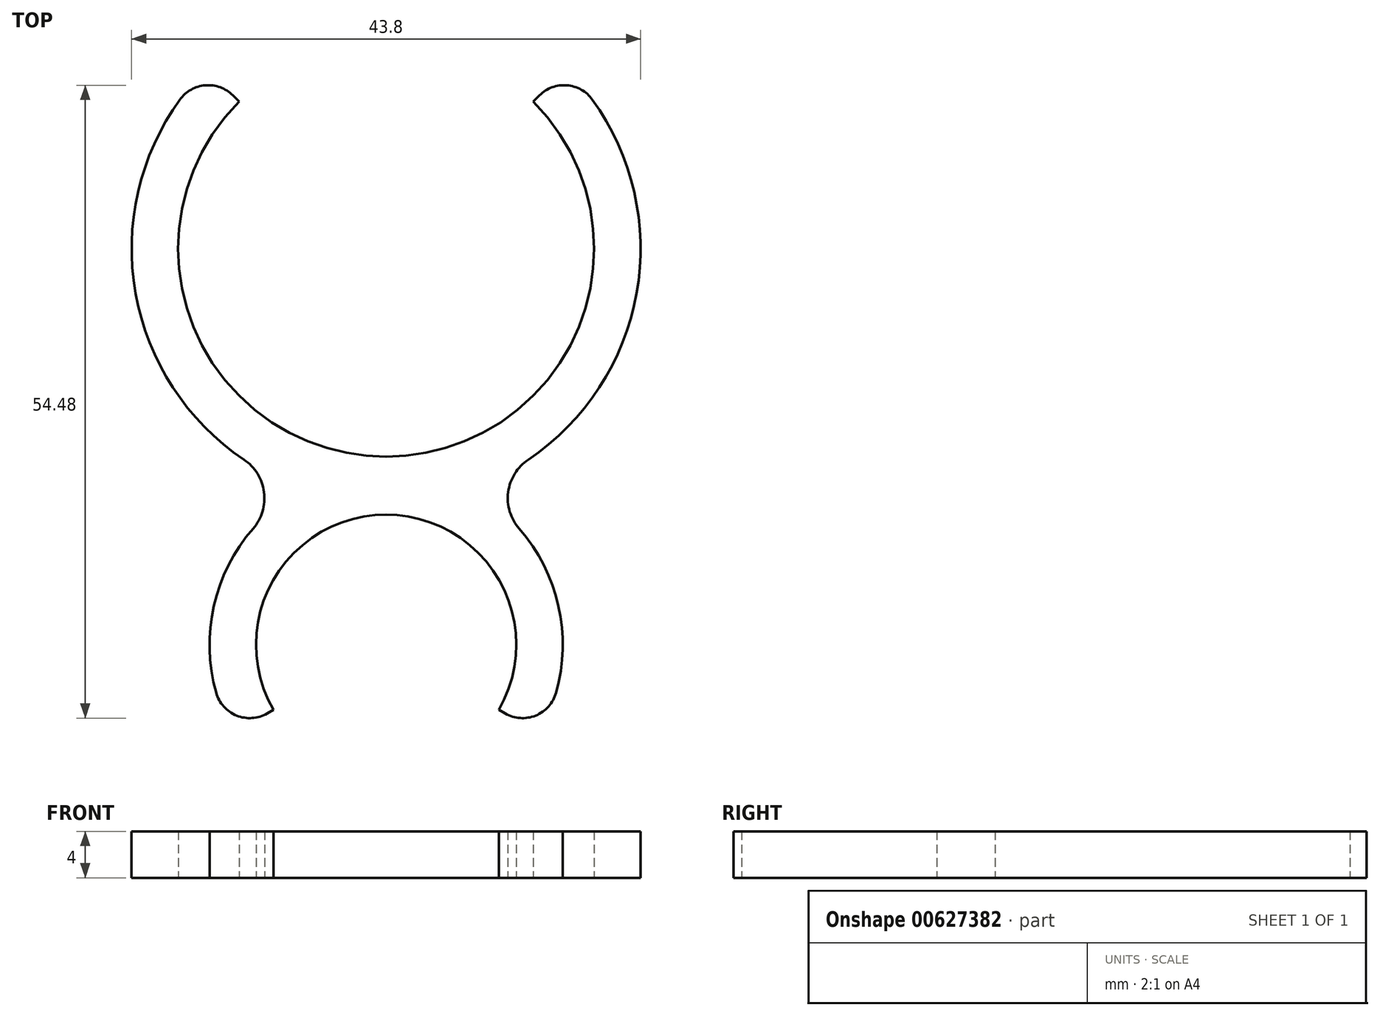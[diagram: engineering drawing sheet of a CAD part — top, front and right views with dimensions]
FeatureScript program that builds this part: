
annotation { "Feature Type Name" : "Feature", "Feature Type Description" : "" }
export const myFeature = defineFeature(function(context is Context, id is Id, definition is map)
    precondition{}
    {
        {
            var Q0;
            Q0=qCreatedBy(makeId("Top.planeOp"),FACE);
            var sketch = newSketch(context, id + "F0", { "sketchPlane" : qUnion([Q0])});
            skLineSegment(sketch, "E0", {"start": v(0, 20.4) * mm, "end": v(0, -13.7) * mm, "construction": true});
            skArc(sketch, "E1", {"start": v(-12.66, 33.06) * mm, "mid": v(0, 2.5) * mm, "end": v(12.66, 33.06) * mm});
            skArc(sketch, "E2", {"start": v(9.7, -19.3) * mm, "mid": v(0, -2.5) * mm, "end": v(-9.7, -19.3) * mm});
            skLineSegment(sketch, "E3", {"start": v(0, -2.5) * mm, "end": v(0, 2.5) * mm, "construction": true});
            skArc(sketch, "E4", {"start": v(-11.46, -3.7) * mm, "mid": v(-14.83, -10.37) * mm, "end": v(-14.63, -17.83) * mm});
            skArc(sketch, "E5", {"start": v(12.24, 2.24) * mm, "mid": v(21.56, 16.57) * mm, "end": v(17.75, 33.23) * mm});
            skPoint(sketch, "E6.visualSharp", {"position": v(-7.17, -0.3) * mm});
            skArc(sketch, "E6.filletArc", {"start": v(-11.46, -3.7) * mm, "mid": v(-10.5, -0.56) * mm, "end": v(-12.24, 2.24) * mm});
            skPoint(sketch, "E7.visualSharp", {"position": v(7.17, -0.3) * mm});
            skArc(sketch, "E7.filletArc", {"start": v(12.24, 2.24) * mm, "mid": v(10.5, -0.56) * mm, "end": v(11.46, -3.7) * mm});
            skLineSegment(sketch, "E8", {"start": v(0, -13.7) * mm, "end": v(-10.24, -19.61) * mm});
            skLineSegment(sketch, "E9", {"start": v(0, 20.4) * mm, "end": v(-13.2, 33.6) * mm});
            skArc(sketch, "E10.MirrorC", {"start": v(-9.7, -19.3) * mm, "mid": v(0, -2.5) * mm, "end": v(9.7, -19.3) * mm});
            skArc(sketch, "E11.MirrorC", {"start": v(12.66, 33.06) * mm, "mid": v(0, 2.5) * mm, "end": v(-12.66, 33.06) * mm});
            skLineSegment(sketch, "E12.MirrorCS", {"start": v(12.66, 33.06) * mm, "end": v(13.2, 33.6) * mm});
            skLineSegment(sketch, "E13.MirrorCS", {"start": v(9.7, -19.3) * mm, "end": v(10.24, -19.61) * mm});
            skArc(sketch, "E14.trimOffspring", {"start": v(-17.75, 33.23) * mm, "mid": v(-21.56, 16.57) * mm, "end": v(-12.24, 2.24) * mm});
            skArc(sketch, "E15.trimOffspring", {"start": v(14.63, -17.83) * mm, "mid": v(14.83, -10.37) * mm, "end": v(11.46, -3.7) * mm});
            skPoint(sketch, "E16.visualSharp", {"position": v(-15.49, 35.89) * mm});
            skArc(sketch, "E16.filletArc", {"start": v(-13.2, 33.6) * mm, "mid": v(-15.56, 34.46) * mm, "end": v(-17.75, 33.23) * mm});
            skPoint(sketch, "E17.visualSharp", {"position": v(15.49, 35.89) * mm});
            skArc(sketch, "E17.filletArc", {"start": v(17.75, 33.23) * mm, "mid": v(15.56, 34.46) * mm, "end": v(13.2, 33.6) * mm});
            skPoint(sketch, "E18.visualSharp", {"position": v(-13.16, -21.3) * mm});
            skArc(sketch, "E18.filletArc", {"start": v(-14.63, -17.83) * mm, "mid": v(-12.87, -19.8) * mm, "end": v(-10.24, -19.61) * mm});
            skPoint(sketch, "E19.visualSharp", {"position": v(13.16, -21.3) * mm});
            skArc(sketch, "E19.filletArc", {"start": v(10.24, -19.61) * mm, "mid": v(12.87, -19.8) * mm, "end": v(14.63, -17.83) * mm});
            skSolve(sketch);
        }
        {
            var Q0;
            Q0=qCreatedBy(makeId("Front.planeOp"),FACE);
            var sketch = newSketch(context, id + "F1", { "sketchPlane" : qUnion([Q0])});
            skLineSegment(sketch, "E20.bottom", {"start": v(-1, -5) * mm, "end": v(1, -5) * mm});
            skLineSegment(sketch, "E20.top", {"start": v(-1, 5) * mm, "end": v(1, 5) * mm});
            skLineSegment(sketch, "E20.left", {"start": v(-2, -4) * mm, "end": v(-2, 4) * mm});
            skLineSegment(sketch, "E20.right", {"start": v(2, -4) * mm, "end": v(2, 4) * mm});
            skPoint(sketch, "E20.middle", {"position": v(0, 0) * mm});
            skLineSegment(sketch, "E21.bottom", {"start": v(5, 5) * mm, "end": v(5, 5) * mm});
            skLineSegment(sketch, "E21.top", {"start": v(5, -5) * mm, "end": v(5, -5) * mm});
            skLineSegment(sketch, "E21.left", {"start": v(6, 4) * mm, "end": v(6, -4) * mm});
            skLineSegment(sketch, "E21.right", {"start": v(4, 4) * mm, "end": v(4, -4) * mm});
            skPoint(sketch, "E21.middle", {"position": v(5, 0) * mm});
            skPoint(sketch, "E22.visualSharp", {"position": v(6, 5) * mm});
            skArc(sketch, "E22.filletArc", {"start": v(6, 4) * mm, "mid": v(5.7, 4.7) * mm, "end": v(5, 5) * mm});
            skPoint(sketch, "E23.visualSharp", {"position": v(4, 5) * mm});
            skArc(sketch, "E23.filletArc", {"start": v(5, 5) * mm, "mid": v(4.3, 4.7) * mm, "end": v(4, 4) * mm});
            skPoint(sketch, "E24.visualSharp", {"position": v(6, -5) * mm});
            skArc(sketch, "E24.filletArc", {"start": v(5, -5) * mm, "mid": v(5.7, -4.7) * mm, "end": v(6, -4) * mm});
            skPoint(sketch, "E25.visualSharp", {"position": v(4, -5) * mm});
            skArc(sketch, "E25.filletArc", {"start": v(4, -4) * mm, "mid": v(4.3, -4.7) * mm, "end": v(5, -5) * mm});
            skPoint(sketch, "E26.visualSharp", {"position": v(2, -5) * mm});
            skArc(sketch, "E26.filletArc", {"start": v(1, -5) * mm, "mid": v(1.7, -4.7) * mm, "end": v(2, -4) * mm});
            skPoint(sketch, "E27.visualSharp", {"position": v(-2, -5) * mm});
            skArc(sketch, "E27.filletArc", {"start": v(-2, -4) * mm, "mid": v(-1.7, -4.7) * mm, "end": v(-1, -5) * mm});
            skPoint(sketch, "E28.visualSharp", {"position": v(2, 5) * mm});
            skArc(sketch, "E28.filletArc", {"start": v(2, 4) * mm, "mid": v(1.7, 4.7) * mm, "end": v(1, 5) * mm});
            skPoint(sketch, "E29.visualSharp", {"position": v(-2, 5) * mm});
            skArc(sketch, "E29.filletArc", {"start": v(-1, 5) * mm, "mid": v(-1.7, 4.7) * mm, "end": v(-2, 4) * mm});
            skLineSegment(sketch, "E30.MirrorCS", {"start": v(-4, 4) * mm, "end": v(-4, -4) * mm});
            skPoint(sketch, "E31.MirrorP", {"position": v(-4, 5) * mm});
            skArc(sketch, "E32.MirrorCS", {"start": v(-6, 4) * mm, "mid": v(-5.7, 4.7) * mm, "end": v(-5, 5) * mm});
            skLineSegment(sketch, "E33.MirrorCS", {"start": v(-6, 4) * mm, "end": v(-6, -4) * mm});
            skArc(sketch, "E34.MirrorCS", {"start": v(-5, 5) * mm, "mid": v(-4.3, 4.7) * mm, "end": v(-4, 4) * mm});
            skArc(sketch, "E35.MirrorCS", {"start": v(-5, -5) * mm, "mid": v(-5.7, -4.7) * mm, "end": v(-6, -4) * mm});
            skArc(sketch, "E36.MirrorCS", {"start": v(-4, -4) * mm, "mid": v(-4.3, -4.7) * mm, "end": v(-5, -5) * mm});
            skSolve(sketch);
        }
        {
            var Q0;
            Q0=makeQuery(id+"F0.imprint","IMPRINT",FACE,{"disambiguationData":[TD([[makeQuery(id+"F0.imprint","IMPRINT",EDGE,{"derivedFrom":sQuery(id+"F0.wireOp",EDGE,"E4")}),1.0]])]});
            extrude(context, id + "F2", {"entities" : qUnion([Q0]), "endBound" : BoundingType.SYMMETRIC, "depth" : 4 * mm, "offsetDistance" : 25 * mm});
        }
    });
